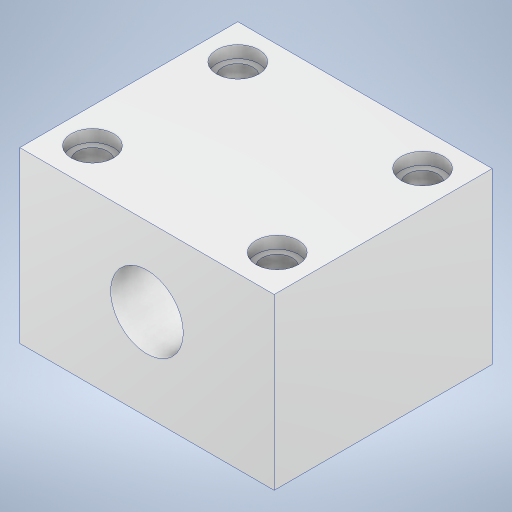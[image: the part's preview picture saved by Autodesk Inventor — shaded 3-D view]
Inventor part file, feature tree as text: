
AUTODESK INVENTOR PART (.ipt)
format: ipt  version: 2023.2 (Build 272271000, 271)  size: 232,960 bytes
history: native  units: mm
features: sketch x2, extrude x1, hole x1, projected_geometry x1
ambient origin geometry x8: Origin, YZ Plane, XZ Plane, XY Plane, X Axis, Y Axis, Z Axis, Center Point
bodies: Solid1 (feature_tree)
feature tree (5):
  extrude  "Extrusion1"  Depth=28.0mm
  hole  "Hole1"  [1 undecoded]
  sketch  "Sketch1"  dims[d0=42.0mm d2=28.0mm]
  sketch  "Sketch2"  dims[d3=90.0deg d4=12.0mm d5=15.0mm d6=36.0mm d7=0.0mm d8=5.75mm d9=5.75mm d11=12.0mm d12=15.25mm d15=5.0mm d16=6.0mm d17=7.0mm d18=2.0mm d19=90.0deg d20=8.0mm d21=20.594885mm]
  projected_geometry  "Projected Loop1"
note: 1 required parameter value undecoded (feature->parameter linkage not recoverable at this tier; creation-order binding heuristic only, values carry confidence <= 0.55)
